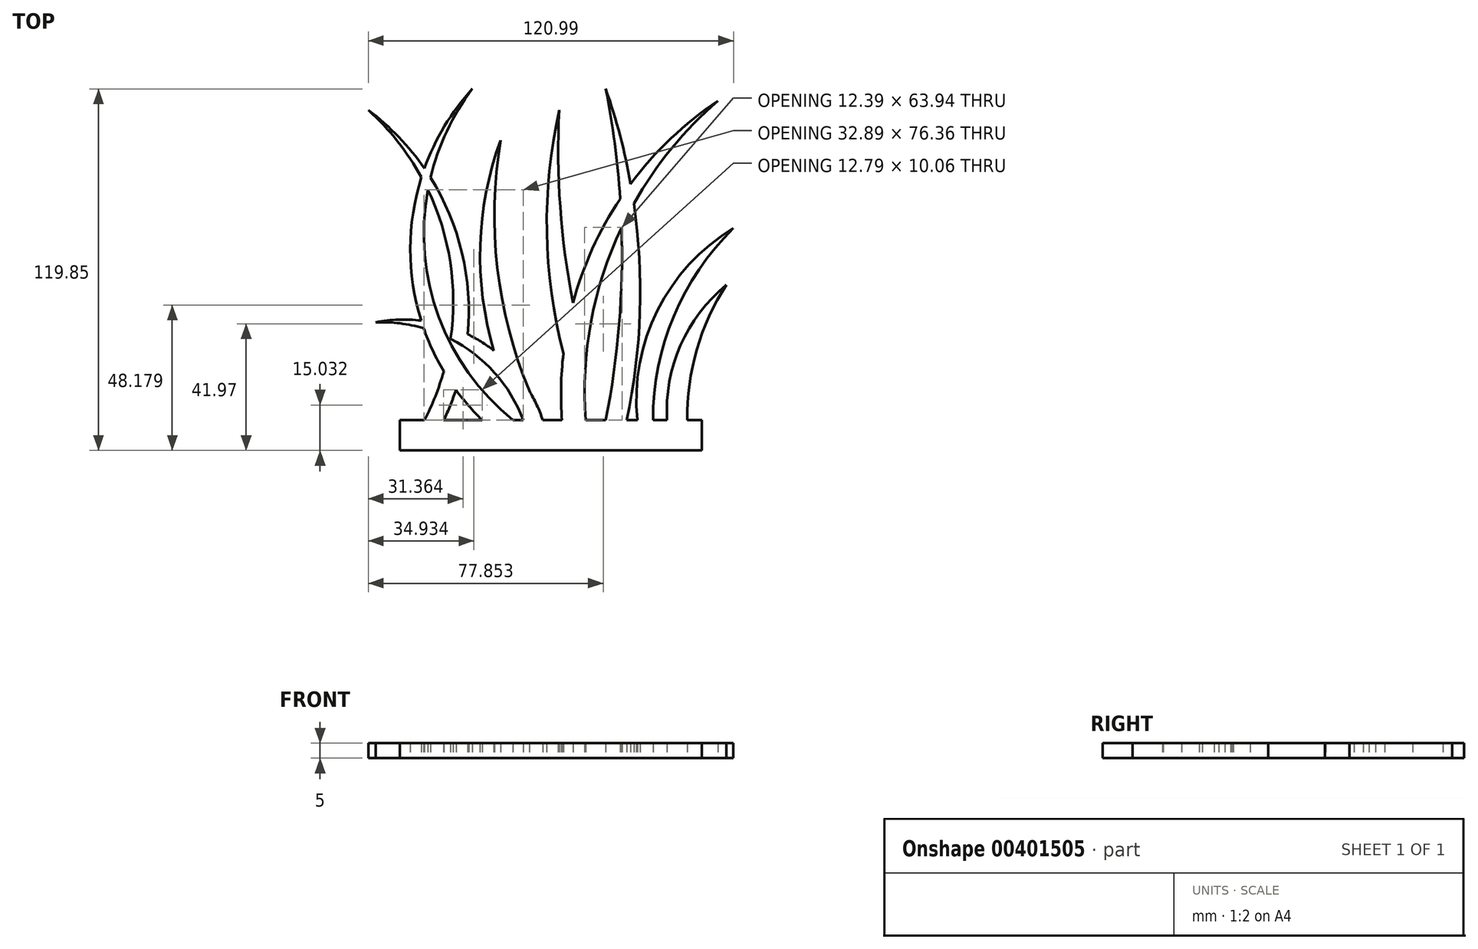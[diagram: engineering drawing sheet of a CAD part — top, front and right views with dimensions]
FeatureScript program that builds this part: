
annotation { "Feature Type Name" : "Feature", "Feature Type Description" : "" }
export const myFeature = defineFeature(function(context is Context, id is Id, definition is map)
    precondition{}
    {
        {
            var Q0;
            Q0=qCreatedBy(makeId("Top.planeOp"),FACE);
            var sketch = newSketch(context, id + "F0", { "sketchPlane" : qUnion([Q0])});
            skLineSegment(sketch, "E0.bottom", {"start": v(0, 0) * mm, "end": v(100, 0) * mm, "construction": true});
            skLineSegment(sketch, "E0.top", {"start": v(0, 100) * mm, "end": v(100, 100) * mm, "construction": true});
            skLineSegment(sketch, "E0.left", {"start": v(0, 0) * mm, "end": v(0, 100) * mm, "construction": true});
            skLineSegment(sketch, "E0.right", {"start": v(100, 0) * mm, "end": v(100, 100) * mm, "construction": true});
            skLineSegment(sketch, "E1.top", {"start": v(0, 10) * mm, "end": v(100, 10) * mm, "construction": true});
            skLineSegment(sketch, "E1.left", {"start": v(0, 0) * mm, "end": v(0, 10) * mm, "construction": true});
            skLineSegment(sketch, "E1.right", {"start": v(100, 0) * mm, "end": v(100, 10) * mm, "construction": true});
            skArc(sketch, "E2", {"start": v(8.14, 10) * mm, "mid": v(16.33, 64.56) * mm, "end": v(-10.45, 112.79) * mm});
            skArc(sketch, "E3", {"start": v(14.52, 10) * mm, "mid": v(20.47, 65.87) * mm, "end": v(-10.45, 112.79) * mm});
            skArc(sketch, "E4", {"start": v(24.02, 119.85) * mm, "mid": v(3.48, 64.26) * mm, "end": v(27.31, 10) * mm});
            skArc(sketch, "E5", {"start": v(24.02, 119.85) * mm, "mid": v(8.53, 62.2) * mm, "end": v(37.46, 10) * mm});
            skArc(sketch, "E6", {"start": v(40.93, 10) * mm, "mid": v(21.7, 34.1) * mm, "end": v(-7.97, 42.47) * mm});
            skArc(sketch, "E7", {"start": v(47.34, 10) * mm, "mid": v(25.83, 36.7) * mm, "end": v(-7.97, 42.47) * mm});
            skArc(sketch, "E8", {"start": v(33.36, 102.73) * mm, "mid": v(26.94, 55.53) * mm, "end": v(40.93, 10) * mm});
            skArc(sketch, "E9", {"start": v(33.36, 102.73) * mm, "mid": v(33.01, 55.26) * mm, "end": v(47.34, 10) * mm});
            skArc(sketch, "E10", {"start": v(105.45, 115.9) * mm, "mid": v(65.27, 69.94) * mm, "end": v(53.72, 10) * mm});
            skArc(sketch, "E11", {"start": v(105.45, 115.9) * mm, "mid": v(70.9, 68.17) * mm, "end": v(61.55, 10) * mm});
            skArc(sketch, "E12", {"start": v(52.8, 112.79) * mm, "mid": v(55.36, 60.62) * mm, "end": v(68.21, 10) * mm});
            skArc(sketch, "E13", {"start": v(52.8, 112.79) * mm, "mid": v(49.29, 60.72) * mm, "end": v(61.55, 10) * mm});
            skArc(sketch, "E14", {"start": v(68.21, 10) * mm, "mid": v(73.6, 64.93) * mm, "end": v(68.21, 119.85) * mm});
            skArc(sketch, "E15", {"start": v(75.16, 10) * mm, "mid": v(79.25, 65.4) * mm, "end": v(68.21, 119.85) * mm});
            skArc(sketch, "E16", {"start": v(110.54, 73.65) * mm, "mid": v(90.76, 44.52) * mm, "end": v(83.89, 10) * mm});
            skArc(sketch, "E17", {"start": v(110.54, 73.65) * mm, "mid": v(85.4, 46.44) * mm, "end": v(78.69, 10) * mm});
            skArc(sketch, "E18", {"start": v(108.22, 54.85) * mm, "mid": v(98.39, 33.4) * mm, "end": v(95.22, 10) * mm});
            skArc(sketch, "E19", {"start": v(108.22, 54.85) * mm, "mid": v(92.98, 34.8) * mm, "end": v(88.54, 10) * mm});
            skLineSegment(sketch, "E20.bottom", {"start": v(0, 10) * mm, "end": v(100, 10) * mm});
            skLineSegment(sketch, "E20.top", {"start": v(0, 0) * mm, "end": v(100, 0) * mm});
            skLineSegment(sketch, "E20.left", {"start": v(0, 10) * mm, "end": v(0, 0) * mm});
            skLineSegment(sketch, "E20.right", {"start": v(100, 10) * mm, "end": v(100, 0) * mm});
            skSolve(sketch);
        }
        {
            var Q0;
            Q0 = qSketchRegion(id + "F0", true);
            var Q1;
            {var subQ0=sQuery(id+"F0.wireOp",EDGE,"E4");var subQ1=sQuery(id+"F0.wireOp",EDGE,"E3");var subQ2=makeQuery(id+"F0.imprint","INTERSECT",VERTEX,{"disambiguationData":[OD(1.0)],"derivedFrom":[subQ1,subQ0]});Q1=makeQuery(id+"F0.imprint","IMPRINT",FACE,{"disambiguationData":[TD([[makeQuery(id+"F0.imprint","IMPRINT",EDGE,{"disambiguationData":[TD([[subQ2,-1.0]])],"derivedFrom":subQ1}),-1.0]])]});}
            var Q2;
            {var subQ0=sQuery(id+"F0.wireOp",EDGE,"E5");var subQ1=sQuery(id+"F0.wireOp",EDGE,"E2");var subQ2=makeQuery(id+"F0.imprint","INTERSECT",VERTEX,{"disambiguationData":[OD(0.0)],"derivedFrom":[subQ1,subQ0]});Q2=makeQuery(id+"F0.imprint","IMPRINT",FACE,{"disambiguationData":[TD([[makeQuery(id+"F0.imprint","IMPRINT",EDGE,{"disambiguationData":[TD([[subQ2,-1.0]])],"derivedFrom":subQ1}),-1.0]])]});}
            extrude(context, id + "F1", {"entities" : qUnion([Q0, Q1, Q2]), "depth" : 5 * mm});
        }
    });
